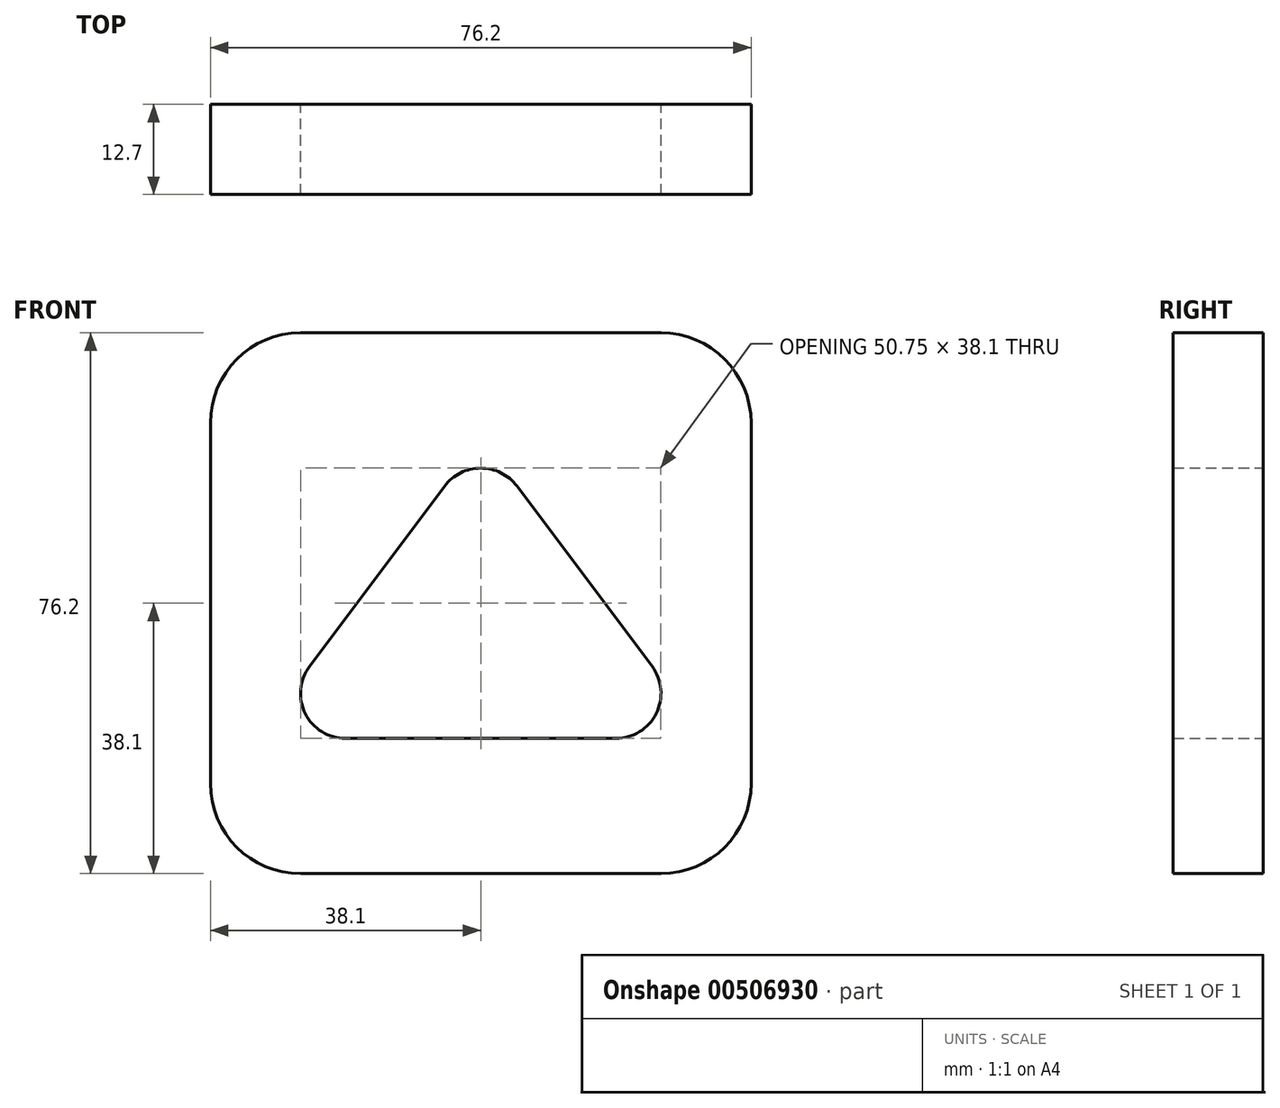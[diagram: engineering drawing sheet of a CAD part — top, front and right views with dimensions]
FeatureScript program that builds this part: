
annotation { "Feature Type Name" : "Feature", "Feature Type Description" : "" }
export const myFeature = defineFeature(function(context is Context, id is Id, definition is map)
    precondition{}
    {
        {
            var Q0;
            Q0=qCreatedBy(makeId("Front.planeOp"),FACE);
            var sketch = newSketch(context, id + "F0", { "sketchPlane" : qUnion([Q0])});
            skLineSegment(sketch, "E0", {"start": v(12.7, 0) * mm, "end": v(63.5, 0) * mm});
            skLineSegment(sketch, "E1", {"start": v(76.2, 12.7) * mm, "end": v(76.2, 63.5) * mm});
            skLineSegment(sketch, "E2", {"start": v(63.5, 76.2) * mm, "end": v(12.7, 76.2) * mm});
            skLineSegment(sketch, "E3", {"start": v(0, 63.5) * mm, "end": v(0, 12.7) * mm});
            skArc(sketch, "E4", {"start": v(13.97, 29.21) * mm, "mid": v(13.37, 22.56) * mm, "end": v(19.05, 19.05) * mm});
            skArc(sketch, "E5", {"start": v(57.15, 19.05) * mm, "mid": v(62.83, 22.56) * mm, "end": v(62.23, 29.21) * mm});
            skArc(sketch, "E6", {"start": v(43.18, 54.6) * mm, "mid": v(38.1, 57.15) * mm, "end": v(33.02, 54.6) * mm});
            skLineSegment(sketch, "E7", {"start": v(33.02, 54.6) * mm, "end": v(13.97, 29.21) * mm});
            skLineSegment(sketch, "E8", {"start": v(43.18, 54.6) * mm, "end": v(62.23, 29.21) * mm});
            skLineSegment(sketch, "E9", {"start": v(19.05, 19.05) * mm, "end": v(57.15, 19.05) * mm});
            skArc(sketch, "E10", {"start": v(12.7, 76.2) * mm, "mid": v(3.72, 72.48) * mm, "end": v(0, 63.5) * mm});
            skPoint(sketch, "E11.orphan", {"position": v(0, 76.2) * mm});
            skArc(sketch, "E12", {"start": v(0, 12.7) * mm, "mid": v(3.72, 3.72) * mm, "end": v(12.7, 0) * mm});
            skArc(sketch, "E13", {"start": v(63.5, 0) * mm, "mid": v(72.48, 3.72) * mm, "end": v(76.2, 12.7) * mm});
            skArc(sketch, "E14", {"start": v(76.2, 63.5) * mm, "mid": v(72.48, 72.48) * mm, "end": v(63.5, 76.2) * mm});
            skSolve(sketch);
        }
        {
            var Q0;
            Q0=makeQuery(id+"F0.imprint","IMPRINT",FACE,{"disambiguationData":[TD([[makeQuery(id+"F0.imprint","IMPRINT",EDGE,{"derivedFrom":sQuery(id+"F0.wireOp",EDGE,"E0")}),1.0]])]});
            extrude(context, id + "F1", {"entities" : qUnion([Q0]), "depth" : 12.7 * mm});
        }
    });
